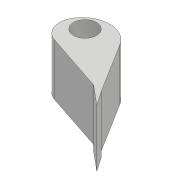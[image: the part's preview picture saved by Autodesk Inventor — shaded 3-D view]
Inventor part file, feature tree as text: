
AUTODESK INVENTOR PART (.ipt)
format: ipt  version: 2017 (Build 210142000, 142)  size: 110,592 bytes
history: native  units: mm
features: fillet x4, extrude x3, sketch x2
ambient origin geometry x8: Origin, YZ Plane, XZ Plane, XY Plane, X Axis, Y Axis, Z Axis, Center Point
bodies: Solid1 (feature_tree)
feature tree (9):
  sketch  "Sketch1"  dims[d0=4.0mm d1=21.0mm d2=9.0mm d3=0.0mm d4=4.75mm d5=4.75mm d6=4.75mm]
  extrude  "Extrusion1"  Depth=4.75mm
  fillet  "Fillet1"  Radius=9.0mm
  fillet  "Fillet2"  Radius=4.75mm
  fillet  "Fillet3"  Radius=4.75mm
  fillet  "Fillet6"  Radius=4.75mm
  extrude  "Extrusion2"  Depth=10.0mm TaperAngle=0.0deg
  extrude  "Extrusion3"  Depth=10.0mm
  sketch  "Sketch2"  dims[d9=3.25mm d10=11.5mm d11=0.0mm d12=3.0mm d13=10.0mm d14=0.0mm]
